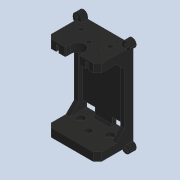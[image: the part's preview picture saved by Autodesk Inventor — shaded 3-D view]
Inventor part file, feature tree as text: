
AUTODESK INVENTOR PART (.ipt)
format: ipt  version: 2020 (Build 240168000, 168)  size: 456,704 bytes
history: native  units: mm
features: extrude x12, sketch x12, mirror x6, chamfer x5, fillet x1, projected_geometry x1
ambient origin geometry x8: Origin, YZ Plane, XZ Plane, XY Plane, X Axis, Y Axis, Z Axis, Center Point
bodies: Solid1 (feature_tree)
feature tree (37):
  extrude  "Extrusion1"  Depth=120.0mm
  extrude  "Extrusion2"  Depth=163.0mm
  extrude  "Extrusion3"  Depth=75.0mm TaperAngle=0.0deg
  extrude  "Extrusion4"  Depth=60.0mm
  chamfer  "Chamfer1"  [1 undecoded]
  chamfer  "Chamfer2"  [1 undecoded]
  chamfer  "Chamfer3"  Distance=20.0mm Angle=45.0deg
  chamfer  "Chamfer4"  Distance=5.0mm Angle=45.0deg
  extrude  "Extrusion7"  Depth=3.0mm TaperAngle=45.0deg
  mirror  "Mirror2"
  extrude  "Extrusion8"  Depth=6.0mm
  mirror  "Mirror3"
  mirror  "Mirror4"
  extrude  "Extrusion9"  Depth=25.0mm
  fillet  "Fillet1"  Radius=32.0mm
  mirror  "Mirror5"
  mirror  "Mirror6"
  extrude  "Extrusion10"  Depth=12.0mm
  mirror  "Mirror7"
  extrude  "Extrusion11"  Depth=20.0mm
  extrude  "Extrusion12"  TaperAngle=0.0deg  [1 undecoded]
  extrude  "Extrusion13"  Depth=20.0mm
  chamfer  "Chamfer5"  Distance=20.0mm
  extrude  "Extrusion14"  Depth=9.0mm
  sketch  "Sketch1"  dims[d0=202.5mm d1=120.0mm]
  sketch  "Sketch2"  dims[d2=85.0mm d3=0.0mm d4=163.0mm]
  sketch  "Sketch3"  dims[d5=10.0mm d6=75.0mm d7=0.0mm]
  sketch  "Sketch4"  dims[d8=13.343mm d9=60.0mm]
  sketch  "Sketch7"  dims[d10=31.0mm]
  sketch  "Sketch9"  dims[d11=0.6mm d12=0.0mm d13=0.0mm]
  sketch  "Sketch10"  dims[d14=20.0mm d17=0.0mm d18=0.0mm d19=20.0mm d20=2.0mm d21=45.0deg d22=5.0mm d23=2.0mm d24=45.0deg]
  sketch  "Sketch11"  dims[d25=1.0mm d26=3.0mm d27=45.0deg d28=1.0mm d29=3.0mm d30=45.0deg]
  sketch  "Sketch12"  dims[d46=6.0mm d47=6.0mm]
  sketch  "Sketch13"  dims[d48=25.0mm d49=14.0mm d50=32.0mm]
  sketch  "Sketch14"  dims[d51=0.0mm d52=0.0mm d57=12.0mm]
  sketch  "Sketch15"  dims[d59=12.0mm d60=20.0mm d61=0.0mm d62=0.0mm d63=20.0mm d64=20.0mm d65=9.0mm d66=5.0mm d67=8.0mm d68=15.0mm d69=0.0mm d70=8.0mm d71=10.0mm d72=12.0mm d73=15.0mm d74=35.0mm d75=20.0mm d76=6.0mm d77=15.0mm d78=0.0mm d79=16.0mm d80=25.0mm d81=11.0mm d82=10.0mm d84=38.402125mm d85=28.75mm d86=0.0mm d87=26.0mm d88=6.0mm d89=13.0mm d90=22.0mm d91=3.0mm d92=0.0mm d93=31.0mm d94=31.0mm d95=5.0mm d96=5.0mm d97=5.0mm d98=5.0mm d99=15.5mm d100=15.5mm d101=15.0mm d102=60.0mm d103=38.402125mm d104=0.0mm d105=0.0mm d106=10.0mm d107=2.0mm d108=45.0deg d109=18.0mm d110=10.0mm d111=0.0mm]
  projected_geometry  "Project Cut Edges1"
note: 3 required parameter values undecoded (feature->parameter linkage not recoverable at this tier; creation-order binding heuristic only, values carry confidence <= 0.55)
